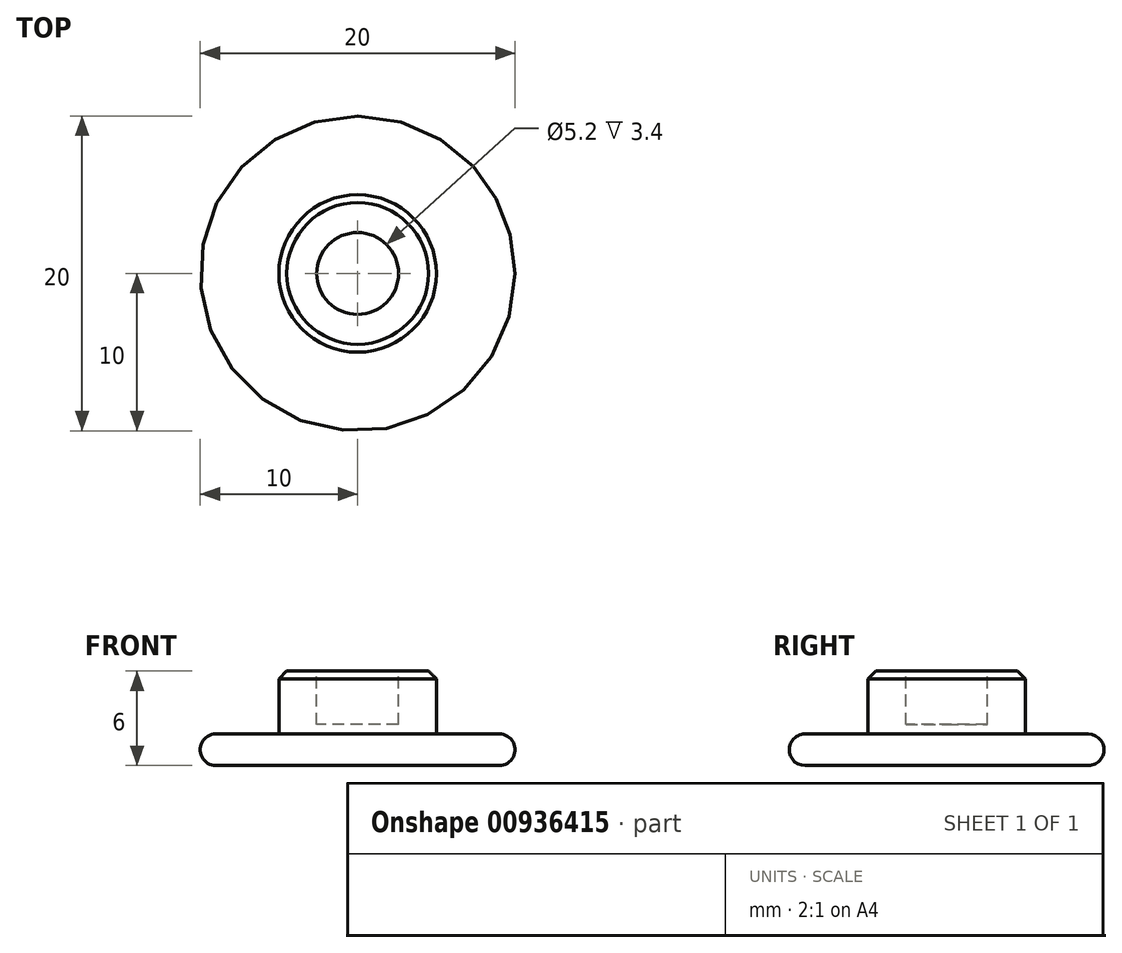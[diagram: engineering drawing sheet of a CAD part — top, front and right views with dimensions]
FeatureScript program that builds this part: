
annotation { "Feature Type Name" : "Feature", "Feature Type Description" : "" }
export const myFeature = defineFeature(function(context is Context, id is Id, definition is map)
    precondition{}
    {
        {
            var Q0;
            Q0=qCreatedBy(makeId("Top.planeOp"),FACE);
            var sketch = newSketch(context, id + "F0", { "sketchPlane" : qUnion([Q0])});
            skCircle(sketch, "E0", {"center": v(0, 0) * mm, "radius": 10 * mm});
            skSolve(sketch);
        }
        {
            var Q0;
            Q0=qSketchRegion(id+"F0",true);
            extrude(context, id + "F1", {"entities" : qUnion([Q0]), "depth" : 2 * mm, "offsetDistance" : 25 * mm});
        }
        {
            var Q0;
            Q0=makeQuery(id+"F1.opExtrude","CAP_FACE",FACE,{"disambiguationData":[OSD([sQuery(id+"F0.wireOp",EDGE,"E0")])],"isStart":false});
            var sketch = newSketch(context, id + "F2", { "sketchPlane" : qUnion([Q0])});
            skCircle(sketch, "E1", {"center": v(0, 0) * mm, "radius": 5 * mm});
            skSolve(sketch);
        }
        {
            var Q0;
            Q0=qSketchRegion(id+"F2",true);
            extrude(context, id + "F3", {"entities" : qUnion([Q0]), "operationType" : NewBodyOperationType.ADD, "depth" : 4 * mm, "offsetDistance" : 25 * mm});
        }
        {
            var Q0;
            Q0=makeQuery(id+"F3.opExtrude","CAP_EDGE",EDGE,{"disambiguationData":[OSD([sQuery(id+"F2.wireOp",EDGE,"E1")])],"isStart":false});
            chamfer(context, id + "F4", {"entities" : qUnion([Q0]), "width" : .5 * mm, "tangentPropagation" : true});
        }
        {
            var Q0;
            Q0=makeQuery(id+"F1.opExtrude","CAP_EDGE",EDGE,{"disambiguationData":[OSD([sQuery(id+"F0.wireOp",EDGE,"E0")])],"isStart":true});
            var Q1;
            Q1=makeQuery(id+"F1.opExtrude","CAP_EDGE",EDGE,{"disambiguationData":[OSD([sQuery(id+"F0.wireOp",EDGE,"E0")])],"isStart":false});
            fillet(context, id + "F5", {"entities" : qUnion([Q0, Q1]), "radius" : 1 * mm, "tangentPropagation" : true, "allowEdgeOverflow" : false});
        }
        {
            var Q0;
            Q0=makeQuery(id+"F3.opExtrude","CAP_FACE",FACE,{"disambiguationData":[OSD([sQuery(id+"F2.wireOp",EDGE,"E1")])],"isStart":false});
            var sketch = newSketch(context, id + "F6", { "sketchPlane" : qUnion([Q0])});
            skCircle(sketch, "E2", {"center": v(0, 0) * mm, "radius": 2.6 * mm});
            skSolve(sketch);
        }
        {
            var Q0;
            Q0=qSketchRegion(id+"F6",true);
            extrude(context, id + "F7", {"entities" : qUnion([Q0]), "operationType" : NewBodyOperationType.REMOVE, "oppositeDirection" : true, "depth" : 3.4 * mm, "offsetDistance" : 25 * mm});
        }
    });
